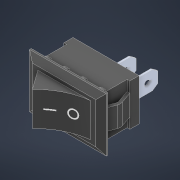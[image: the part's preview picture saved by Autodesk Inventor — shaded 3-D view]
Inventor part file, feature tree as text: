
AUTODESK INVENTOR PART (.ipt)
format: ipt  version: 2021 (Build 250183000, 183)  size: 219,648 bytes
history: native  units: mm
features: chamfer x1
ambient origin geometry x8: Origin, YZ Plane, XZ Plane, XY Plane, X Axis, Y Axis, Z Axis, Center Point
bodies: Solid1 (feature_tree)
feature tree (1):
  chamfer  "Chamfer2"  [1 undecoded]
note: 1 required parameter value undecoded (feature->parameter linkage not recoverable at this tier; creation-order binding heuristic only, values carry confidence <= 0.55)
